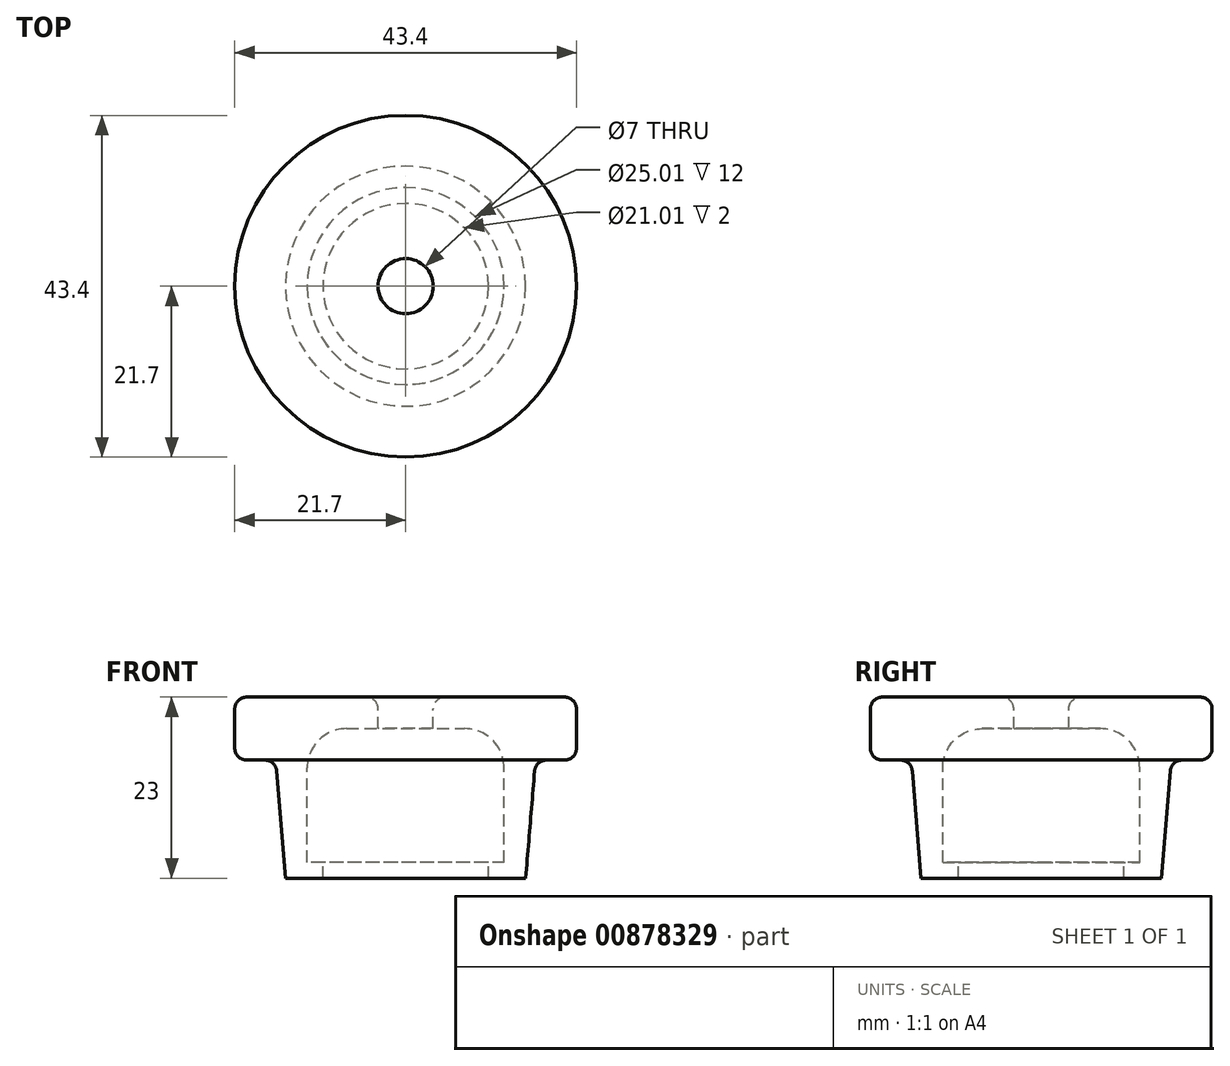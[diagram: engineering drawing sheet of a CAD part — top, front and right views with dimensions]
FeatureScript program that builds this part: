
annotation { "Feature Type Name" : "Feature", "Feature Type Description" : "" }
export const myFeature = defineFeature(function(context is Context, id is Id, definition is map)
    precondition{}
    {
        {
            var Q0;
            Q0=qCreatedBy(makeId("Front.planeOp"),FACE);
            var sketch = newSketch(context, id + "F0", { "sketchPlane" : qUnion([Q0])});
            skLineSegment(sketch, "E0", {"start": v(3.5, 11.5) * mm, "end": v(21.7, 11.5) * mm});
            skLineSegment(sketch, "E1", {"start": v(21.7, 11.5) * mm, "end": v(21.7, 3.5) * mm});
            skLineSegment(sketch, "E2", {"start": v(21.7, 3.5) * mm, "end": v(16.5, 3.5) * mm});
            skLineSegment(sketch, "E3", {"start": v(16.5, 3.5) * mm, "end": v(15.25, -11.5) * mm});
            skLineSegment(sketch, "E4", {"start": v(15.25, -11.5) * mm, "end": v(10.5, -11.5) * mm});
            skLineSegment(sketch, "E5", {"start": v(10.5, -11.5) * mm, "end": v(10.5, -9.5) * mm});
            skLineSegment(sketch, "E6", {"start": v(10.5, -9.5) * mm, "end": v(12.5, -9.5) * mm});
            skLineSegment(sketch, "E7", {"start": v(12.5, -9.5) * mm, "end": v(12.5, 7.5) * mm});
            skLineSegment(sketch, "E8", {"start": v(12.5, 7.5) * mm, "end": v(3.5, 7.5) * mm});
            skLineSegment(sketch, "E9", {"start": v(3.5, 7.5) * mm, "end": v(3.5, 11.5) * mm});
            skLineSegment(sketch, "E10", {"start": v(0, 33.53) * mm, "end": v(0, -46.16) * mm, "construction": true});
            skSolve(sketch);
        }
        {
            var Q0;
            Q0 = qSketchRegion(id + "F0", true);
            var Q1;
            Q1=sQuery(id+"F0.wireOp",EDGE,"E10");
            revolve(context, id + "F1", {"surfaceOperationType" : NewSurfaceOperationType.NEW, "entities" : qUnion([Q0]), "axis" : qUnion([Q1]), "revolveType" : RevolveType.FULL});
        }
        {
            var Q0;
            Q0=makeQuery(id+"F1.opRevolve","SWEPT_EDGE",EDGE,{"disambiguationData":[OSD([sQuery(id+"F0.wireOp",EDGE,"E0"),sQuery(id+"F0.wireOp",EDGE,"E9")])]});
            var Q1;
            Q1=makeQuery(id+"F1.opRevolve","SWEPT_EDGE",EDGE,{"disambiguationData":[OSD([sQuery(id+"F0.wireOp",EDGE,"E0"),sQuery(id+"F0.wireOp",EDGE,"E1")])]});
            var Q2;
            Q2=makeQuery(id+"F1.opRevolve","SWEPT_EDGE",EDGE,{"disambiguationData":[OSD([sQuery(id+"F0.wireOp",EDGE,"E1"),sQuery(id+"F0.wireOp",EDGE,"E2")])]});
            var Q3;
            Q3=makeQuery(id+"F1.opRevolve","SWEPT_EDGE",EDGE,{"disambiguationData":[OSD([sQuery(id+"F0.wireOp",EDGE,"E2"),sQuery(id+"F0.wireOp",EDGE,"E3")])]});
            fillet(context, id + "F2", {"entities" : qUnion([Q0, Q1, Q2, Q3]), "radius" : 1.5 * mm, "tangentPropagation" : true, "allowEdgeOverflow" : false});
        }
        {
            var Q0;
            Q0=makeQuery(id+"F1.opRevolve","SWEPT_EDGE",EDGE,{"disambiguationData":[OSD([sQuery(id+"F0.wireOp",EDGE,"E7"),sQuery(id+"F0.wireOp",EDGE,"E8")])]});
            fillet(context, id + "F3", {"entities" : qUnion([Q0]), "radius" : 5 * mm, "tangentPropagation" : true, "allowEdgeOverflow" : false});
        }
    });
